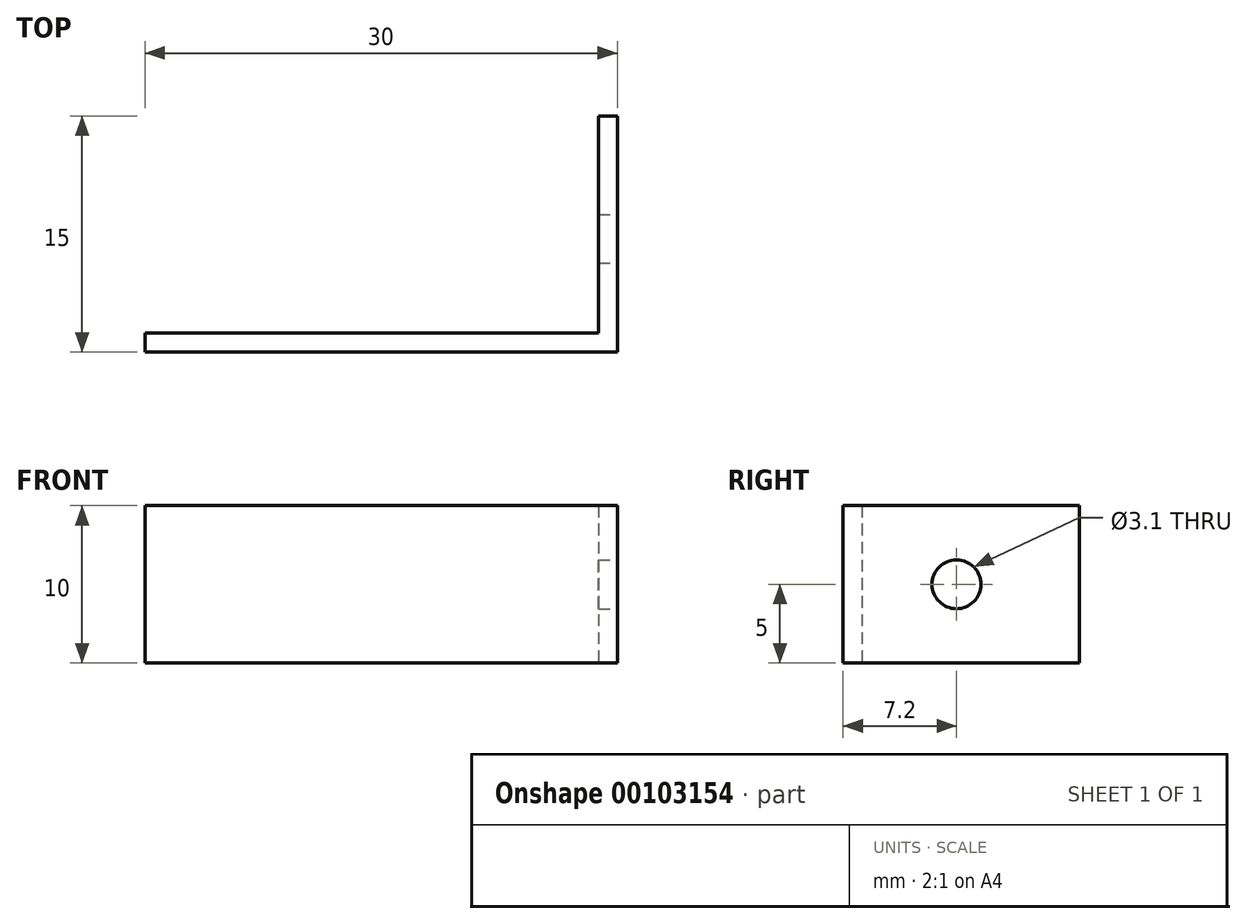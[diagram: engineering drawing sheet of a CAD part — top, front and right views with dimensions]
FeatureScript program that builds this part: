
annotation { "Feature Type Name" : "Feature", "Feature Type Description" : "" }
export const myFeature = defineFeature(function(context is Context, id is Id, definition is map)
    precondition{}
    {
        {
            var Q0;
            Q0=qCreatedBy(makeId("Top.planeOp"),FACE);
            var sketch = newSketch(context, id + "F0", { "sketchPlane" : qUnion([Q0])});
            skLineSegment(sketch, "E0", {"start": v(-5.72, 0) * mm, "end": v(23.08, 0) * mm});
            skLineSegment(sketch, "E1", {"start": v(23.08, 0) * mm, "end": v(23.08, 13.8) * mm});
            skLineSegment(sketch, "E2", {"start": v(23.08, 13.8) * mm, "end": v(24.28, 13.8) * mm});
            skLineSegment(sketch, "E3", {"start": v(24.28, 13.8) * mm, "end": v(24.28, -1.2) * mm});
            skLineSegment(sketch, "E4", {"start": v(24.28, -1.2) * mm, "end": v(-5.72, -1.2) * mm});
            skLineSegment(sketch, "E5", {"start": v(-5.72, -1.2) * mm, "end": v(-5.72, 0) * mm});
            skSolve(sketch);
        }
        {
            var Q0;
            Q0 = qSketchRegion(id + "F0", true);
            extrude(context, id + "F1", {"entities" : qUnion([Q0]), "depth" : 10 * mm});
        }
        {
            var Q0;
            Q0=makeQuery(id+"F1.opExtrude","SWEPT_FACE",FACE,{"disambiguationData":[OSD([sQuery(id+"F0.wireOp",EDGE,"E3")])]});
            var sketch = newSketch(context, id + "F2", { "sketchPlane" : qUnion([Q0])});
            skCircle(sketch, "E6", {"center": v(6, 5) * mm, "radius": 1.55 * mm});
            skSolve(sketch);
        }
        {
            var Q0;
            Q0 = qSketchRegion(id + "F2", true);
            extrude(context, id + "F3", {"entities" : qUnion([Q0]), "operationType" : NewBodyOperationType.REMOVE, "oppositeDirection" : true, "depth" : 1.2 * mm});
        }
    });
